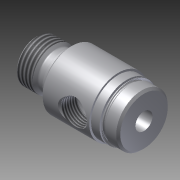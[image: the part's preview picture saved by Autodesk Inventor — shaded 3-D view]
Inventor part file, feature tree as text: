
AUTODESK INVENTOR PART (.ipt)
format: ipt  version: 2012 (Build 160160000, 160)  size: 265,728 bytes
history: native  units: in
note: dims shown in document units (in); Inventor stores cm internally (conversion verified against a paired STEP export)
features: other x105, sketch x6, revolve x5, thread x2, hole x1
ambient origin geometry x8: Origin, YZ Plane, XZ Plane, XY Plane, X Axis, Y Axis, Z Axis, Center Point
bodies: Solid1 (feature_tree)
feature tree (119):
  revolve  "Revolution1"  [1 undecoded]
  thread  "Thread1"  [1 undecoded]
  revolve  "Revolution2"  Angle=360.0deg
  hole  "Drilling 1"  [1 undecoded]
  revolve  "Revolution3"  [1 undecoded]
  revolve  "Revolution4"  [1 undecoded]
  thread  "Thread2"  [1 undecoded]
  revolve  "Revolution5"  [1 undecoded]
  other  "s1_XY"
  other  "s1_YZ"
  other  "s1_ZX"
  other  "s1_X"
  other  "s1_Y"
  other  "s1_Z"
  other  "s1_Center"
  other  "s2_XY"
  other  "s2_YZ"
  other  "s2_ZX"
  other  "s2_X"
  other  "s2_Y"
  other  "s2_Z"
  other  "s2_Center"
  other  "dp1_XY"
  other  "dp1_YZ"
  other  "dp1_ZX"
  other  "dp1_X"
  other  "dp1_Y"
  other  "dp1_Z"
  other  "dp1_Center"
  other  "dp2_XY"
  other  "dp2_YZ"
  other  "dp2_ZX"
  other  "dp2_X"
  other  "dp2_Y"
  other  "dp2_Z"
  other  "dp2_Center"
  other  "rod_guide_XY"
  other  "rod_guide_YZ"
  other  "rod_guide_ZX"
  other  "rod_guide_X"
  other  "rod_guide_Y"
  other  "rod_guide_Z"
  other  "rod_guide_Center"
  other  "to_tube_XY"
  other  "to_tube_YZ"
  other  "to_tube_ZX"
  other  "to_tube_X"
  other  "to_tube_Y"
  other  "to_tube_Z"
  other  "to_tube_Center"
  other  "to_foot_bracket_XY"
  other  "to_foot_bracket_YZ"
  other  "to_foot_bracket_ZX"
  other  "to_foot_bracket_X"
  other  "to_foot_bracket_Y"
  other  "to_foot_bracket_Z"
  other  "to_foot_bracket_Center"
  other  "to_nut_XY"
  other  "to_nut_YZ"
  other  "to_nut_ZX"
  other  "to_nut_X"
  other  "to_nut_Y"
  other  "to_nut_Z"
  other  "to_nut_Center"
  other  "to_trunnion_brackets_XY"
  other  "to_trunnion_brackets_YZ"
  other  "to_trunnion_brackets_ZX"
  other  "to_trunnion_brackets_X"
  other  "to_trunnion_brackets_Y"
  other  "to_trunnion_brackets_Z"
  other  "to_trunnion_brackets_Center"
  other  "to_trunnion_brackets1_XY"
  other  "to_trunnion_brackets1_YZ"
  other  "to_trunnion_brackets1_ZX"
  other  "to_trunnion_brackets1_X"
  other  "to_trunnion_brackets1_Y"
  other  "to_trunnion_brackets1_Z"
  other  "to_trunnion_brackets1_Center"
  other  "to_trunnion_brackets2_XY"
  other  "to_trunnion_brackets2_YZ"
  other  "to_trunnion_brackets2_ZX"
  other  "to_trunnion_brackets2_X"
  other  "to_trunnion_brackets2_Y"
  other  "to_trunnion_brackets2_Z"
  other  "to_trunnion_brackets2_Center"
  other  "t111_XY"
  other  "t111_YZ"
  other  "t111_ZX"
  other  "t111_X"
  other  "t111_Y"
  other  "t111_Z"
  other  "t111_Center"
  other  "t1_XY"
  other  "t1_YZ"
  other  "t1_ZX"
  other  "t1_X"
  other  "t1_Y"
  other  "t1_Z"
  other  "t1_Center"
  other  "port_XY"
  other  "port_YZ"
  other  "port_ZX"
  other  "port_X"
  other  "port_Y"
  other  "port_Z"
  other  "port_Center"
  other  "to_screw_XY"
  other  "to_screw_YZ"
  other  "to_screw_ZX"
  other  "to_screw_X"
  other  "to_screw_Y"
  other  "to_screw_Z"
  other  "to_screw_Center"
  sketch  "Sketch_2"  dims[d0=360.0deg d1=0.23in d2=0.0in d3=360.0deg]
  sketch  "Sketch_3"  dims[d4=0.2535in d5=0.75in d6=0.2735in d7=0.25in d8=90.0deg d9=1.594in d10=0.0in d11=360.0deg]
  sketch  "Sketch3"  dims[d12=360.0deg d13=0.1252in d14=0.0in]
  sketch  "Sketch_10"  dims[d15=360.0deg]
  sketch  "Sketch_40"
  sketch  "Sketch_47"
note: 7 required parameter values undecoded (feature->parameter linkage not recoverable at this tier; creation-order binding heuristic only, values carry confidence <= 0.55)